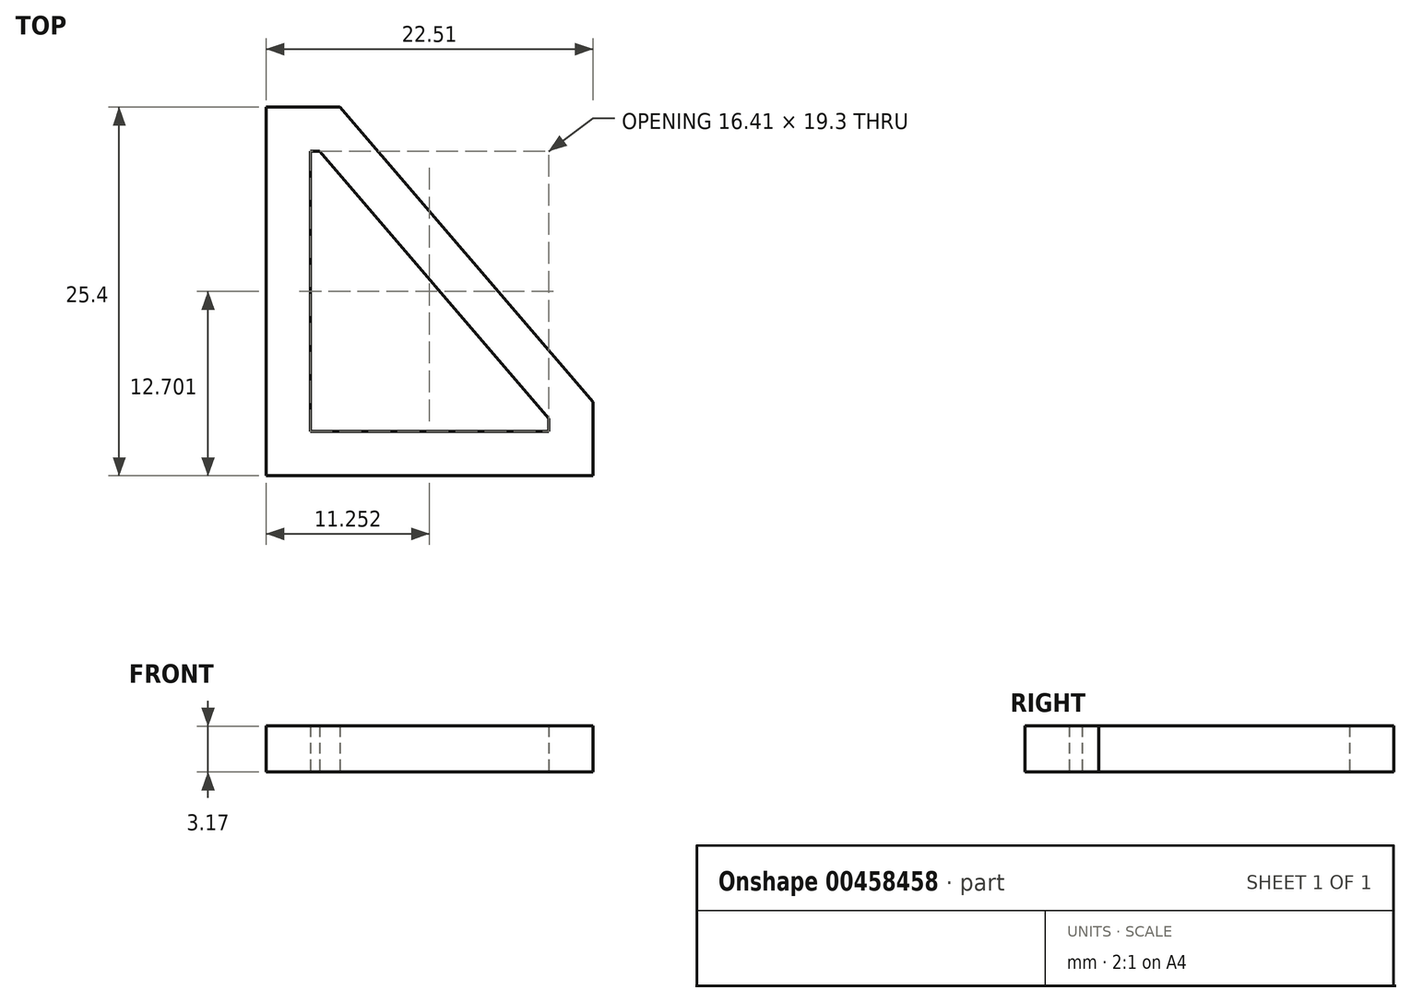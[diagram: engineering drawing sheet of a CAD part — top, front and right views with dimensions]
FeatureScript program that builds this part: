
annotation { "Feature Type Name" : "Feature", "Feature Type Description" : "" }
export const myFeature = defineFeature(function(context is Context, id is Id, definition is map)
    precondition{}
    {
        {
            var Q0;
            Q0=qCreatedBy(makeId("Top.planeOp"),FACE);
            var sketch = newSketch(context, id + "F0", { "sketchPlane" : qUnion([Q0])});
            skLineSegment(sketch, "E0", {"start": v(-58.38, 56.4) * mm, "end": v(-58.38, 31) * mm});
            skLineSegment(sketch, "E1", {"start": v(-58.38, 31) * mm, "end": v(-35.87, 31) * mm});
            skLineSegment(sketch, "E2", {"start": v(-35.87, 31) * mm, "end": v(-35.87, 36.07) * mm});
            skLineSegment(sketch, "E3", {"start": v(-35.87, 36.07) * mm, "end": v(-53.3, 56.4) * mm});
            skLineSegment(sketch, "E4", {"start": v(-53.3, 56.4) * mm, "end": v(-58.38, 56.4) * mm});
            skLineSegment(sketch, "E5.0", {"start": v(-38.92, 34.94) * mm, "end": v(-54.7, 53.34) * mm});
            skLineSegment(sketch, "E5.1", {"start": v(-38.92, 34.04) * mm, "end": v(-38.92, 34.94) * mm});
            skLineSegment(sketch, "E5.2", {"start": v(-54.7, 53.34) * mm, "end": v(-55.33, 53.34) * mm});
            skLineSegment(sketch, "E5.3", {"start": v(-55.33, 53.34) * mm, "end": v(-55.33, 34.04) * mm});
            skLineSegment(sketch, "E5.4", {"start": v(-55.33, 34.04) * mm, "end": v(-38.92, 34.04) * mm});
            skSolve(sketch);
        }
        {
            var Q0;
            Q0=makeQuery(id+"F0.imprint","IMPRINT",FACE,{"disambiguationData":[TD([[makeQuery(id+"F0.imprint","IMPRINT",EDGE,{"derivedFrom":sQuery(id+"F0.wireOp",EDGE,"E0")}),1.0]])]});
            extrude(context, id + "F1", {"entities" : qUnion([Q0]), "depth" : 3.17 * mm});
        }
    });
